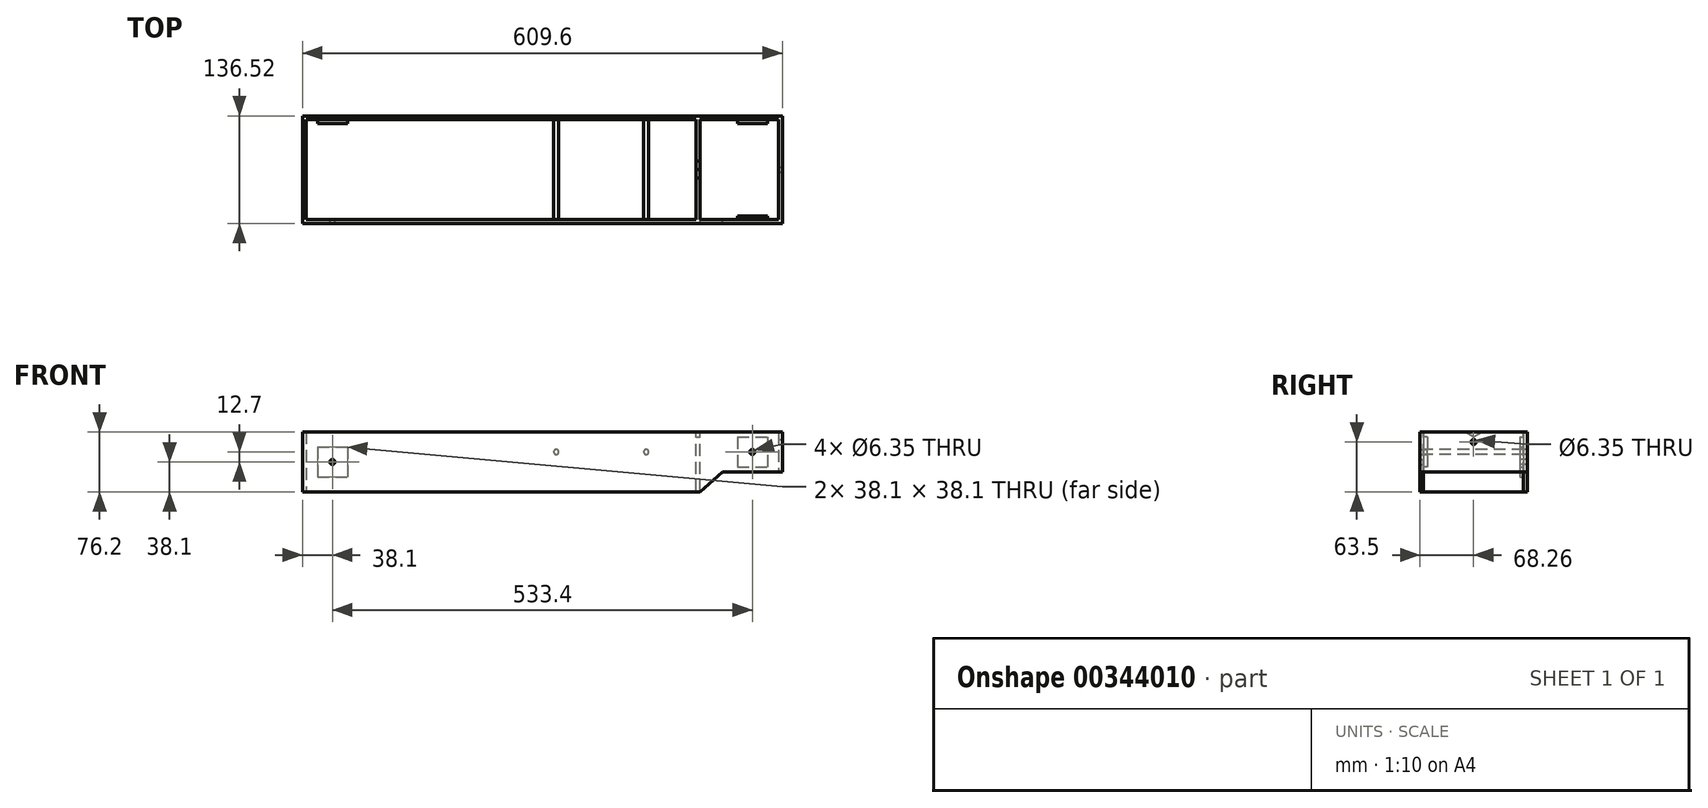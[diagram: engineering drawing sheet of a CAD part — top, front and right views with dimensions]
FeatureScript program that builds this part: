
annotation { "Feature Type Name" : "Feature", "Feature Type Description" : "" }
export const myFeature = defineFeature(function(context is Context, id is Id, definition is map)
    precondition{}
    {
        {
            var Q0;
            Q0=qCreatedBy(makeId("Front.planeOp"),FACE);
            var sketch = newSketch(context, id + "F0", { "sketchPlane" : qUnion([Q0])});
            skLineSegment(sketch, "E0", {"start": v(0, 0) * mm, "end": v(505, 0) * mm});
            skLineSegment(sketch, "E1", {"start": v(505, 0) * mm, "end": v(533.4, 25.4) * mm});
            skLineSegment(sketch, "E2", {"start": v(533.4, 25.4) * mm, "end": v(609.6, 25.4) * mm});
            skLineSegment(sketch, "E3", {"start": v(609.6, 25.4) * mm, "end": v(609.6, 76.2) * mm});
            skLineSegment(sketch, "E4", {"start": v(609.6, 76.2) * mm, "end": v(0, 76.2) * mm});
            skLineSegment(sketch, "E5", {"start": v(0, 76.2) * mm, "end": v(0, 0) * mm});
            skCircle(sketch, "E6", {"center": v(571.5, 50.8) * mm, "radius": 3.18 * mm});
            skPoint(sketch, "E6.centerSnap0", {"position": v(609.6, 50.8) * mm});
            skCircle(sketch, "E7", {"center": v(38.1, 38.1) * mm, "radius": 3.18 * mm});
            skPoint(sketch, "E7.centerSnap0", {"position": v(0, 38.1) * mm});
            skSolve(sketch);
        }
        {
            var Q0;
            Q0 = qSketchRegion(id + "F0", true);
            extrude(context, id + "F1", {"entities" : qUnion([Q0]), "depth" : 4.76 * mm});
        }
        {
            var Q0;
            Q0=makeQuery(id+"F1.opExtrude","CAP_FACE",FACE,{"disambiguationData":[OSD([sQuery(id+"F0.wireOp",EDGE,"E0"),sQuery(id+"F0.wireOp",EDGE,"E1"),sQuery(id+"F0.wireOp",EDGE,"E2"),sQuery(id+"F0.wireOp",EDGE,"E3"),sQuery(id+"F0.wireOp",EDGE,"E4"),sQuery(id+"F0.wireOp",EDGE,"E5"),sQuery(id+"F0.wireOp",EDGE,"E6"),sQuery(id+"F0.wireOp",EDGE,"E7")])],"isStart":true});
            var sketch = newSketch(context, id + "F2", { "sketchPlane" : qUnion([Q0])});
            skLineSegment(sketch, "E8.bottom", {"start": v(-609.6, 76.2) * mm, "end": v(-604.84, 76.2) * mm});
            skLineSegment(sketch, "E8.top", {"start": v(-609.6, 25.4) * mm, "end": v(-604.84, 25.4) * mm});
            skLineSegment(sketch, "E8.left", {"start": v(-609.6, 76.2) * mm, "end": v(-609.6, 25.4) * mm});
            skLineSegment(sketch, "E8.right", {"start": v(-604.84, 76.2) * mm, "end": v(-604.84, 25.4) * mm});
            skLineSegment(sketch, "E9.bottom", {"start": v(-505, 0) * mm, "end": v(-500.24, 0) * mm});
            skLineSegment(sketch, "E9.top", {"start": v(-505, 76.2) * mm, "end": v(-500.24, 76.2) * mm});
            skLineSegment(sketch, "E9.left", {"start": v(-505, 0) * mm, "end": v(-505, 76.2) * mm});
            skLineSegment(sketch, "E9.right", {"start": v(-500.24, 0) * mm, "end": v(-500.24, 76.2) * mm});
            skCircle(sketch, "E10", {"center": v(-436.74, 50.8) * mm, "radius": 3.18 * mm});
            skCircle(sketch, "E11", {"center": v(-322.44, 50.8) * mm, "radius": 3.18 * mm});
            skLineSegment(sketch, "E12.bottom", {"start": v(0, 76.2) * mm, "end": v(-4.76, 76.2) * mm});
            skLineSegment(sketch, "E12.top", {"start": v(0, 0) * mm, "end": v(-4.76, 0) * mm});
            skLineSegment(sketch, "E12.left", {"start": v(0, 76.2) * mm, "end": v(0, 0) * mm});
            skLineSegment(sketch, "E12.right", {"start": v(-4.76, 76.2) * mm, "end": v(-4.76, 0) * mm});
            skSolve(sketch);
        }
        {
            var Q0;
            Q0 = qSketchRegion(id + "F2", true);
            extrude(context, id + "F3", {"entities" : qUnion([Q0]), "operationType" : NewBodyOperationType.ADD, "depth" : 127 * mm});
        }
        {
            var Q0;
            Q0=makeQuery(id+"F3.opExtrude","CAP_FACE",FACE,{"disambiguationData":[OSD([sQuery(id+"F2.wireOp",EDGE,"E8.bottom"),sQuery(id+"F2.wireOp",EDGE,"E8.top"),sQuery(id+"F2.wireOp",EDGE,"E8.left"),sQuery(id+"F2.wireOp",EDGE,"E8.right")])],"isStart":false});
            var sketch = newSketch(context, id + "F4", { "sketchPlane" : qUnion([Q0])});
            skLineSegment(sketch, "E13", {"start": v(-609.6, 76.2) * mm, "end": v(0, 76.2) * mm});
            skLineSegment(sketch, "E14", {"start": v(0, 76.2) * mm, "end": v(0, 0) * mm});
            skLineSegment(sketch, "E15", {"start": v(0, 0) * mm, "end": v(-505, 0) * mm});
            skLineSegment(sketch, "E16", {"start": v(-505, 0) * mm, "end": v(-533.4, 25.4) * mm});
            skLineSegment(sketch, "E17", {"start": v(-533.4, 25.4) * mm, "end": v(-609.6, 25.4) * mm});
            skLineSegment(sketch, "E18", {"start": v(-609.6, 25.4) * mm, "end": v(-609.6, 76.2) * mm});
            skCircle(sketch, "E19", {"center": v(-571.5, 50.8) * mm, "radius": 3.18 * mm});
            skPoint(sketch, "E19.centerSnap0", {"position": v(-604.84, 50.8) * mm});
            skCircle(sketch, "E20", {"center": v(-38.1, 38.1) * mm, "radius": 3.18 * mm});
            skPoint(sketch, "E20.centerSnap0", {"position": v(0, 38.1) * mm});
            skSolve(sketch);
        }
        {
            var Q0;
            Q0 = qSketchRegion(id + "F4", true);
            extrude(context, id + "F5", {"entities" : qUnion([Q0]), "operationType" : NewBodyOperationType.ADD, "depth" : 4.76 * mm});
        }
        {
            var Q0;
            Q0=makeQuery(id+"F5.boolean.opBoolean","MERGE",FACE,{"derivedFrom":[makeQuery(id+"F3.boolean.opBoolean","MERGE",FACE,{"derivedFrom":[makeQuery(id+"F1.opExtrude","SWEPT_FACE",FACE,{"disambiguationData":[OSD([sQuery(id+"F0.wireOp",EDGE,"E3")])]}),makeQuery(id+"F3.opExtrude","SWEPT_FACE",FACE,{"disambiguationData":[OSD([sQuery(id+"F2.wireOp",EDGE,"E8.left")])]})]}),makeQuery(id+"F5.opExtrude","SWEPT_FACE",FACE,{"disambiguationData":[OSD([sQuery(id+"F4.wireOp",EDGE,"E18")])]})]});
            var sketch = newSketch(context, id + "F6", { "sketchPlane" : qUnion([Q0])});
            skCircle(sketch, "E21", {"center": v(63.5, 63.5) * mm, "radius": 3.18 * mm});
            skPoint(sketch, "E21.centerSnap0", {"position": v(63.5, 76.2) * mm});
            skSolve(sketch);
        }
        {
            var Q0;
            Q0 = qSketchRegion(id + "F6", true);
            extrude(context, id + "F7", {"entities" : qUnion([Q0]), "operationType" : NewBodyOperationType.REMOVE, "oppositeDirection" : true, "depth" : 25.4 * mm});
        }
        {
            var Q0;
            Q0=makeQuery(id+"F3.opExtrude","SWEPT_FACE",FACE,{"disambiguationData":[OSD([sQuery(id+"F2.wireOp",EDGE,"E9.left")])]});
            var sketch = newSketch(context, id + "F8", { "sketchPlane" : qUnion([Q0])});
            skLineSegment(sketch, "E22", {"start": v(63.5, 76.2) * mm, "end": v(63.5, 69.85) * mm});
            skLineSegment(sketch, "E23", {"start": v(63.5, 69.85) * mm, "end": v(74.5, 76.2) * mm});
            skLineSegment(sketch, "E24", {"start": v(63.5, 69.85) * mm, "end": v(52.5, 76.2) * mm});
            skLineSegment(sketch, "E25", {"start": v(52.5, 76.2) * mm, "end": v(74.5, 76.2) * mm});
            skSolve(sketch);
        }
        {
            var Q0;
            Q0 = qSketchRegion(id + "F8", true);
            extrude(context, id + "F9", {"entities" : qUnion([Q0]), "operationType" : NewBodyOperationType.REMOVE, "oppositeDirection" : true, "depth" : 25.4 * mm});
        }
        {
            var Q0;
            {var subQ0=sQuery(id+"F0.wireOp",EDGE,"E0");var subQ1=sQuery(id+"F0.wireOp",EDGE,"E4");var subQ2=sQuery(id+"F0.wireOp",EDGE,"E7");Q0=makeQuery(id+"F3.boolean.opBoolean","SPLIT",FACE,{"disambiguationData":[TD([makeQuery(id+"F1.opExtrude","SWEPT_FACE",FACE,{"disambiguationData":[OSD([subQ2])]})])],"derivedFrom":makeQuery(id+"F1.opExtrude","CAP_FACE",FACE,{"disambiguationData":[OSD([subQ0,sQuery(id+"F0.wireOp",EDGE,"E1"),sQuery(id+"F0.wireOp",EDGE,"E2"),sQuery(id+"F0.wireOp",EDGE,"E3"),subQ1,sQuery(id+"F0.wireOp",EDGE,"E5"),sQuery(id+"F0.wireOp",EDGE,"E6"),subQ2])],"isStart":true})});}
            var sketch = newSketch(context, id + "F10", { "sketchPlane" : qUnion([Q0])});
            skLineSegment(sketch, "E26.bottom", {"start": v(-57.15, 57.15) * mm, "end": v(-19.05, 57.15) * mm});
            skLineSegment(sketch, "E26.top", {"start": v(-57.15, 19.05) * mm, "end": v(-19.05, 19.05) * mm});
            skLineSegment(sketch, "E26.left", {"start": v(-57.15, 57.15) * mm, "end": v(-57.15, 19.05) * mm});
            skLineSegment(sketch, "E26.right", {"start": v(-19.05, 57.15) * mm, "end": v(-19.05, 19.05) * mm});
            skSolve(sketch);
        }
        {
            var Q0;
            Q0=makeQuery(id+"F10.imprint","IMPRINT",FACE,{"disambiguationData":[TD([[makeQuery(id+"F10.imprint","IMPRINT",EDGE,{"derivedFrom":sQuery(id+"F10.wireOp",EDGE,"E26.bottom")}),-1.0]])]});
            extrude(context, id + "F11", {"entities" : qUnion([Q0]), "operationType" : NewBodyOperationType.ADD, "depth" : 3 / 406.4 * mm});
        }
        {
            var Q0;
            {var subQ0=sQuery(id+"F0.wireOp",EDGE,"E2");var subQ1=sQuery(id+"F0.wireOp",EDGE,"E6");var subQ2=sQuery(id+"F0.wireOp",EDGE,"E0");var subQ3=sQuery(id+"F0.wireOp",EDGE,"E1");var subQ4=sQuery(id+"F0.wireOp",EDGE,"E4");Q0=makeQuery(id+"F3.boolean.opBoolean","SPLIT",FACE,{"disambiguationData":[TD([makeQuery(id+"F1.opExtrude","SWEPT_FACE",FACE,{"disambiguationData":[OSD([subQ3])]})])],"derivedFrom":makeQuery(id+"F1.opExtrude","CAP_FACE",FACE,{"disambiguationData":[OSD([subQ2,subQ3,subQ0,sQuery(id+"F0.wireOp",EDGE,"E3"),subQ4,sQuery(id+"F0.wireOp",EDGE,"E5"),subQ1,sQuery(id+"F0.wireOp",EDGE,"E7")])],"isStart":true})});}
            var sketch = newSketch(context, id + "F12", { "sketchPlane" : qUnion([Q0])});
            skLineSegment(sketch, "E27.bottom", {"start": v(-590.55, 69.85) * mm, "end": v(-552.45, 69.85) * mm});
            skLineSegment(sketch, "E27.top", {"start": v(-590.55, 31.75) * mm, "end": v(-552.45, 31.75) * mm});
            skLineSegment(sketch, "E27.left", {"start": v(-590.55, 69.85) * mm, "end": v(-590.55, 31.75) * mm});
            skLineSegment(sketch, "E27.right", {"start": v(-552.45, 69.85) * mm, "end": v(-552.45, 31.75) * mm});
            skSolve(sketch);
        }
        {
            var Q0;
            Q0=makeQuery(id+"F12.imprint","IMPRINT",FACE,{"disambiguationData":[TD([[makeQuery(id+"F12.imprint","IMPRINT",EDGE,{"derivedFrom":sQuery(id+"F12.wireOp",EDGE,"E27.bottom")}),-1.0]])]});
            extrude(context, id + "F13", {"entities" : qUnion([Q0]), "operationType" : NewBodyOperationType.ADD, "depth" : 4.76 * mm});
        }
        {
            var Q0;
            {var subQ1=sQuery(id+"F4.wireOp",EDGE,"E14");Q0=makeQuery(id+"F4.imprint","IMPRINT",FACE,{"disambiguationData":[TD([[makeQuery(id+"F4.imprint","IMPRINT",EDGE,{"derivedFrom":subQ1}),-1.0]])]});}
            var sketch = newSketch(context, id + "F14", { "sketchPlane" : qUnion([Q0])});
            skLineSegment(sketch, "E28.bottom", {"start": v(-19.05, 57.15) * mm, "end": v(-57.15, 57.15) * mm});
            skLineSegment(sketch, "E28.top", {"start": v(-19.05, 19.05) * mm, "end": v(-57.15, 19.05) * mm});
            skLineSegment(sketch, "E28.left", {"start": v(-19.05, 57.15) * mm, "end": v(-19.05, 19.05) * mm});
            skLineSegment(sketch, "E28.right", {"start": v(-57.15, 57.15) * mm, "end": v(-57.15, 19.05) * mm});
            skSolve(sketch);
        }
        {
            var Q0;
            Q0=makeQuery(id+"F14.imprint","IMPRINT",FACE,{"disambiguationData":[TD([[makeQuery(id+"F14.imprint","IMPRINT",EDGE,{"derivedFrom":sQuery(id+"F14.wireOp",EDGE,"E28.bottom")}),1.0]])]});
            extrude(context, id + "F15", {"entities" : qUnion([Q0]), "operationType" : NewBodyOperationType.ADD, "oppositeDirection" : true, "depth" : 4.76 * mm});
        }
        {
            var Q0;
            {var subQ1=sQuery(id+"F4.wireOp",EDGE,"E14");Q0=makeQuery(id+"F4.imprint","IMPRINT",FACE,{"disambiguationData":[TD([[makeQuery(id+"F4.imprint","IMPRINT",EDGE,{"derivedFrom":subQ1}),-1.0]])]});}
            var sketch = newSketch(context, id + "F16", { "sketchPlane" : qUnion([Q0])});
            skLineSegment(sketch, "E29.bottom", {"start": v(-552.45, 69.85) * mm, "end": v(-590.55, 69.85) * mm});
            skLineSegment(sketch, "E29.top", {"start": v(-552.45, 31.75) * mm, "end": v(-590.55, 31.75) * mm});
            skLineSegment(sketch, "E29.left", {"start": v(-552.45, 69.85) * mm, "end": v(-552.45, 31.75) * mm});
            skLineSegment(sketch, "E29.right", {"start": v(-590.55, 69.85) * mm, "end": v(-590.55, 31.75) * mm});
            skSolve(sketch);
        }
        {
            var Q0;
            Q0=makeQuery(id+"F16.imprint","IMPRINT",FACE,{"disambiguationData":[TD([[makeQuery(id+"F16.imprint","IMPRINT",EDGE,{"derivedFrom":sQuery(id+"F16.wireOp",EDGE,"E29.bottom")}),1.0]])]});
            extrude(context, id + "F17", {"entities" : qUnion([Q0]), "operationType" : NewBodyOperationType.ADD, "oppositeDirection" : true, "depth" : 4.76 * mm});
        }
    });
